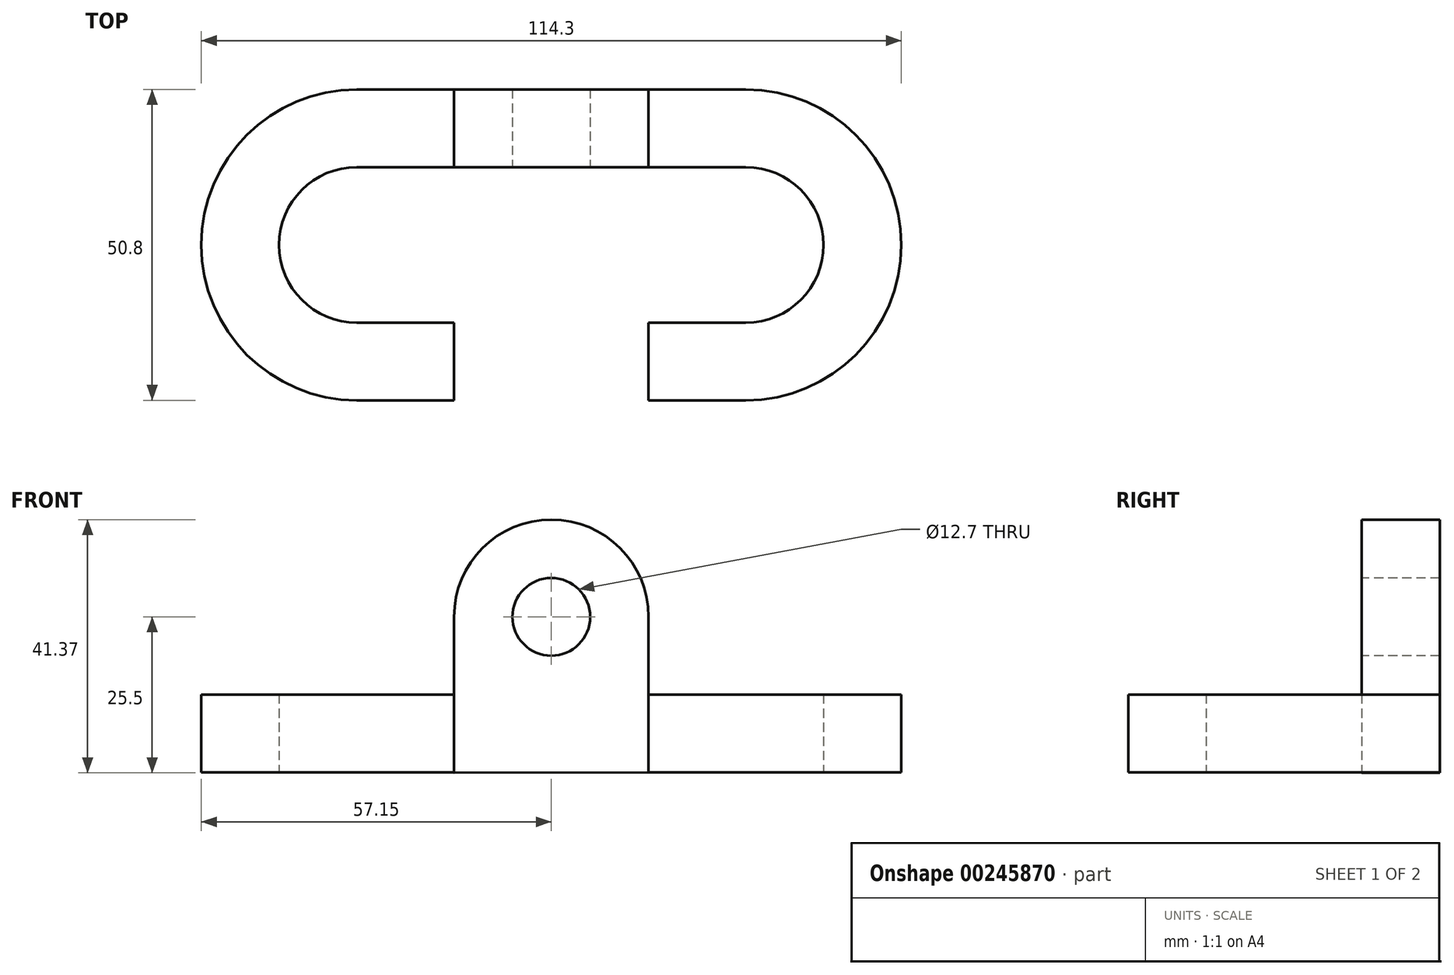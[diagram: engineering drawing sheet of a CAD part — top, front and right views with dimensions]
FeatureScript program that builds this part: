
annotation { "Feature Type Name" : "Feature", "Feature Type Description" : "" }
export const myFeature = defineFeature(function(context is Context, id is Id, definition is map)
    precondition{}
    {
        {
            var Q0;
            Q0=qCreatedBy(makeId("Top.planeOp"),FACE);
            var sketch = newSketch(context, id + "F0", { "sketchPlane" : qUnion([Q0])});
            skArc(sketch, "E0", {"start": v(31.75, -25.4) * mm, "mid": v(57.15, 0) * mm, "end": v(31.75, 25.4) * mm});
            skArc(sketch, "E1", {"start": v(31.75, -12.7) * mm, "mid": v(44.45, 0) * mm, "end": v(31.75, 12.7) * mm});
            skLineSegment(sketch, "E2", {"start": v(31.75, 0) * mm, "end": v(31.75, 53.88) * mm, "construction": true});
            skLineSegment(sketch, "E3", {"start": v(31.75, 12.7) * mm, "end": v(0, 12.7) * mm});
            skLineSegment(sketch, "E4", {"start": v(31.75, 25.4) * mm, "end": v(0, 25.4) * mm});
            skLineSegment(sketch, "E5", {"start": v(31.75, -25.4) * mm, "end": v(15.88, -25.4) * mm});
            skLineSegment(sketch, "E6", {"start": v(31.75, -12.7) * mm, "end": v(15.88, -12.7) * mm});
            skLineSegment(sketch, "E7", {"start": v(15.88, -12.7) * mm, "end": v(15.88, -25.4) * mm});
            skPoint(sketch, "E8.orphan", {"position": v(0, -12.7) * mm});
            skPoint(sketch, "E9.orphan", {"position": v(0, -25.4) * mm});
            skArc(sketch, "E10.MirrorCS", {"start": v(-31.75, -12.7) * mm, "mid": v(-44.45, 0) * mm, "end": v(-31.75, 12.7) * mm});
            skLineSegment(sketch, "E11.MirrorCS", {"start": v(-15.88, -12.7) * mm, "end": v(-15.88, -25.4) * mm});
            skLineSegment(sketch, "E12.MirrorCS", {"start": v(-31.75, -25.4) * mm, "end": v(-15.88, -25.4) * mm});
            skLineSegment(sketch, "E13.MirrorCS", {"start": v(-31.75, -12.7) * mm, "end": v(-15.88, -12.7) * mm});
            skLineSegment(sketch, "E14.MirrorCS", {"start": v(-31.75, 25.4) * mm, "end": v(0, 25.4) * mm});
            skLineSegment(sketch, "E15.MirrorCS", {"start": v(-31.75, 12.7) * mm, "end": v(0, 12.7) * mm});
            skArc(sketch, "E16.MirrorCS", {"start": v(-31.75, -25.4) * mm, "mid": v(-57.15, 0) * mm, "end": v(-31.75, 25.4) * mm});
            skSolve(sketch);
        }
        {
            var Q0;
            Q0 = qSketchRegion(id + "F0", true);
            extrude(context, id + "F1", {"entities" : qUnion([Q0]), "depth" : 12.7 * mm});
        }
        {
            var Q0;
            Q0=makeQuery(id+"F1.opExtrude","SWEPT_FACE",FACE,{"disambiguationData":[OSD([sQuery(id+"F0.wireOp",EDGE,"E3"),sQuery(id+"F0.wireOp",EDGE,"E15.MirrorCS")])]});
            var sketch = newSketch(context, id + "F2", { "sketchPlane" : qUnion([Q0])});
            skArc(sketch, "E17", {"start": v(15.88, 25.4) * mm, "mid": v(0, 41.28) * mm, "end": v(-15.88, 25.4) * mm});
            skCircle(sketch, "E18", {"center": v(0, 25.4) * mm, "radius": 6.35 * mm});
            skLineSegment(sketch, "E19", {"start": v(0, 25.4) * mm, "end": v(-37.4, 25.4) * mm, "construction": true});
            skLineSegment(sketch, "E20", {"start": v(-15.88, 25.4) * mm, "end": v(-15.88, -0.1) * mm});
            skLineSegment(sketch, "E21", {"start": v(15.88, 25.4) * mm, "end": v(15.88, 0) * mm});
            skLineSegment(sketch, "E22", {"start": v(-15.87, -0.1) * mm, "end": v(15.88, 0) * mm});
            skSolve(sketch);
        }
        {
            var Q0;
            Q0 = qSketchRegion(id + "F2", true);
            extrude(context, id + "F3", {"entities" : qUnion([Q0]), "operationType" : NewBodyOperationType.ADD, "oppositeDirection" : true, "depth" : 12.7 * mm});
        }
    });
